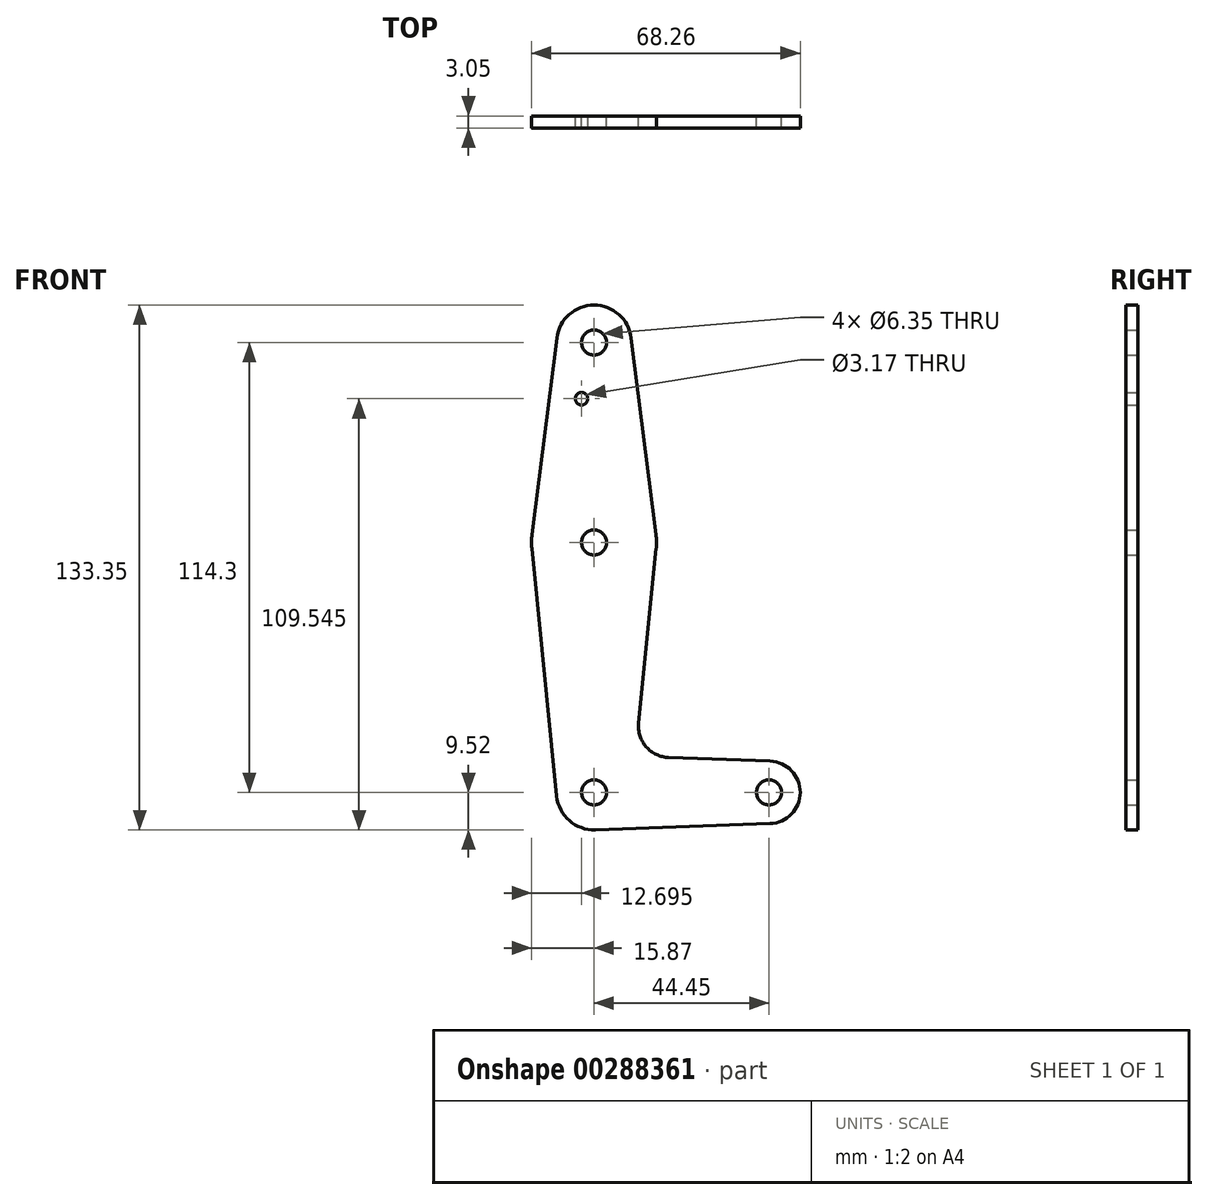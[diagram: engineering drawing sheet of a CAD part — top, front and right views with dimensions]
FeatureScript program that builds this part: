
annotation { "Feature Type Name" : "Feature", "Feature Type Description" : "" }
export const myFeature = defineFeature(function(context is Context, id is Id, definition is map)
    precondition{}
    {
        {
            var Q0;
            Q0=qCreatedBy(makeId("Front.planeOp"),FACE);
            var sketch = newSketch(context, id + "F0", { "sketchPlane" : qUnion([Q0])});
            skCircle(sketch, "E0", {"center": v(0, 0) * mm, "radius": 9.53 * mm});
            skCircle(sketch, "E1", {"center": v(0, 63.5) * mm, "radius": 15.88 * mm});
            skCircle(sketch, "E2", {"center": v(0, 114.3) * mm, "radius": 9.53 * mm});
            skCircle(sketch, "E3", {"center": v(44.45, 0) * mm, "radius": 7.94 * mm});
            skLineSegment(sketch, "E4", {"start": v(9.45, 115.5) * mm, "end": v(15.75, 65.48) * mm});
            skLineSegment(sketch, "E5", {"start": v(-9.45, 115.5) * mm, "end": v(-15.75, 65.48) * mm});
            skLineSegment(sketch, "E6", {"start": v(-15.8, 61.91) * mm, "end": v(-9.48, -0.95) * mm});
            skLineSegment(sketch, "E7", {"start": v(15.8, 61.91) * mm, "end": v(11.34, 17.6) * mm});
            skLineSegment(sketch, "E8", {"start": v(18.97, 8.85) * mm, "end": v(44.73, 7.93) * mm});
            skLineSegment(sketch, "E9", {"start": v(0.34, -9.52) * mm, "end": v(44.73, -7.93) * mm});
            skCircle(sketch, "E10", {"center": v(0, 114.3) * mm, "radius": 3.18 * mm});
            skCircle(sketch, "E11", {"center": v(-3.18, 100.03) * mm, "radius": 1.59 * mm});
            skCircle(sketch, "E12", {"center": v(0, 63.5) * mm, "radius": 3.18 * mm});
            skCircle(sketch, "E13", {"center": v(0, 0) * mm, "radius": 3.18 * mm});
            skCircle(sketch, "E14", {"center": v(44.45, 0) * mm, "radius": 3.18 * mm});
            skArc(sketch, "E15.filletArc", {"start": v(11.34, 17.6) * mm, "mid": v(13.26, 11.57) * mm, "end": v(18.97, 8.85) * mm});
            skSolve(sketch);
        }
        {
            var Q0;
            Q0 = qSketchRegion(id + "F0", true);
            extrude(context, id + "F1", {"entities" : qUnion([Q0]), "depth" : 3.05 * mm});
        }
    });
